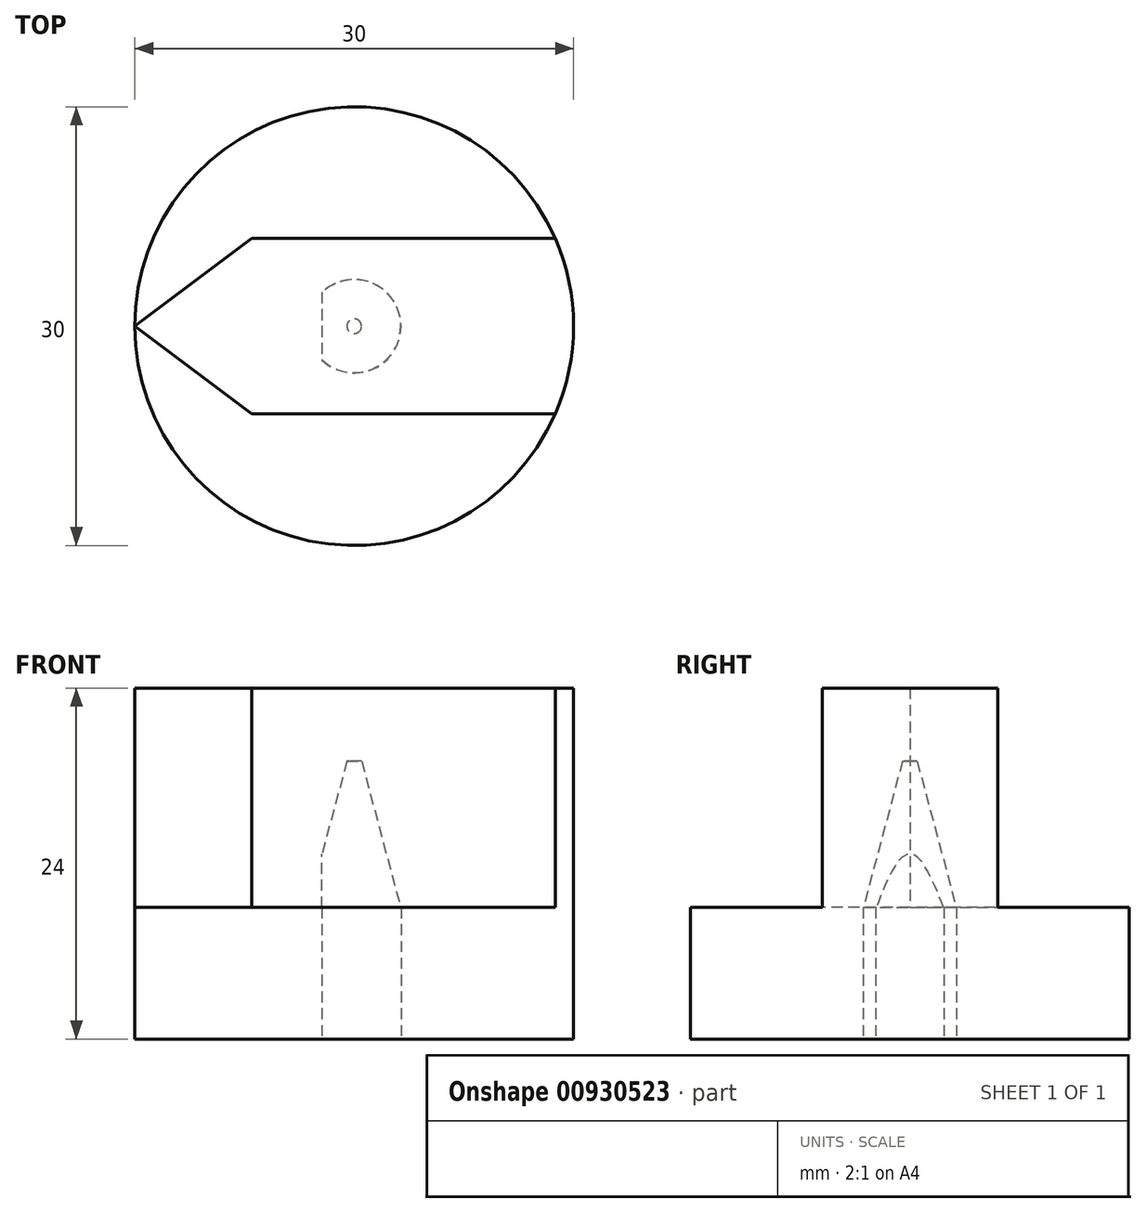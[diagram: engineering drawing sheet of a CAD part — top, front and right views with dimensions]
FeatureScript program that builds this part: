
annotation { "Feature Type Name" : "Feature", "Feature Type Description" : "" }
export const myFeature = defineFeature(function(context is Context, id is Id, definition is map)
    precondition{}
    {
        {
            var Q0;
            Q0=qCreatedBy(makeId("Top.planeOp"),FACE);
            var sketch = newSketch(context, id + "F0", { "sketchPlane" : qUnion([Q0])});
            skCircle(sketch, "E0", {"center": v(0, 0) * mm, "radius": 3.2 * mm, "construction": true});
            skLineSegment(sketch, "E1", {"start": v(-2.2, 2.32) * mm, "end": v(-2.2, -2.32) * mm});
            skLineSegment(sketch, "E2", {"start": v(3.2, 0) * mm, "end": v(-2.2, 0) * mm, "construction": true});
            skArc(sketch, "E3", {"start": v(-2.2, -2.32) * mm, "mid": v(3.2, 0) * mm, "end": v(-2.2, 2.32) * mm});
            skCircle(sketch, "E4", {"center": v(0, 0) * mm, "radius": 15 * mm});
            skSolve(sketch);
        }
        {
            var Q0;
            Q0 = qSketchRegion(id + "F0", true);
            extrude(context, id + "F1", {"entities" : qUnion([Q0]), "depth" : 9 * mm, "offsetDistance" : 25 * mm});
        }
        {
            var Q0;
            Q0=makeQuery(id+"F1.opExtrude","CAP_FACE",FACE,{"disambiguationData":[OSD([sQuery(id+"F0.wireOp",EDGE,"E1"),sQuery(id+"F0.wireOp",EDGE,"E3"),sQuery(id+"F0.wireOp",EDGE,"E4")])],"isStart":false});
            var sketch = newSketch(context, id + "F2", { "sketchPlane" : qUnion([Q0])});
            skLineSegment(sketch, "E5", {"start": v(-15, 0) * mm, "end": v(-7, 6) * mm});
            skLineSegment(sketch, "E6", {"start": v(-7, 6) * mm, "end": v(13.75, 6) * mm});
            skArc(sketch, "E7", {"start": v(15, 0) * mm, "mid": v(14.68, 3.06) * mm, "end": v(13.75, 6) * mm});
            skLineSegment(sketch, "E8", {"start": v(-15, 0) * mm, "end": v(15, 0) * mm, "construction": true});
            skLineSegment(sketch, "E9.MirrorCS", {"start": v(-15, 0) * mm, "end": v(-7, -6) * mm});
            skLineSegment(sketch, "E10.MirrorCS", {"start": v(-7, -6) * mm, "end": v(13.75, -6) * mm});
            skArc(sketch, "E11.MirrorCS", {"start": v(15, 0) * mm, "mid": v(14.68, -3.06) * mm, "end": v(13.75, -6) * mm});
            skCircle(sketch, "E12", {"center": v(0, 0) * mm, "radius": 0.5 * mm});
            skSolve(sketch);
        }
        {
            var Q0;
            Q0 = qSketchRegion(id + "F2", true);
            extrude(context, id + "F3", {"entities" : qUnion([Q0]), "operationType" : NewBodyOperationType.ADD, "depth" : 10 * mm, "offsetDistance" : 25 * mm});
        }
        {
            var Q0;
            Q0=makeQuery(id+"F3.opExtrude","CAP_EDGE",EDGE,{"disambiguationData":[OSD([sQuery(id+"F2.wireOp",EDGE,"E12")])],"isStart":true});
            chamfer(context, id + "F4", {"entities" : qUnion([Q0]), "chamferType" : ChamferType.OFFSET_ANGLE, "width" : 10 * mm, "oppositeDirection" : true, "angle" : 15 * degree, "tangentPropagation" : true});
        }
        {
            var Q0;
            Q0=makeQuery(id+"F3.opExtrude","CAP_FACE",FACE,{"disambiguationData":[OSD([sQuery(id+"F2.wireOp",EDGE,"E5"),sQuery(id+"F2.wireOp",EDGE,"E6"),sQuery(id+"F2.wireOp",EDGE,"E7"),sQuery(id+"F2.wireOp",EDGE,"E9.MirrorCS"),sQuery(id+"F2.wireOp",EDGE,"E10.MirrorCS"),sQuery(id+"F2.wireOp",EDGE,"E11.MirrorCS"),sQuery(id+"F2.wireOp",EDGE,"E12")])],"isStart":false});
            var sketch = newSketch(context, id + "F5", { "sketchPlane" : qUnion([Q0])});
            skLineSegment(sketch, "E13", {"start": v(-15, 0) * mm, "end": v(-7, 6) * mm});
            skLineSegment(sketch, "E14", {"start": v(-7, 6) * mm, "end": v(13.75, 6) * mm});
            skLineSegment(sketch, "E15", {"start": v(-15, 0) * mm, "end": v(-7, -6) * mm});
            skLineSegment(sketch, "E16", {"start": v(-7, -6) * mm, "end": v(13.75, -6) * mm});
            skArc(sketch, "E17", {"start": v(13.75, -6) * mm, "mid": v(15, 0) * mm, "end": v(13.75, 6) * mm});
            skSolve(sketch);
        }
        {
            var Q0;
            Q0 = qSketchRegion(id + "F5", true);
            extrude(context, id + "F6", {"entities" : qUnion([Q0]), "operationType" : NewBodyOperationType.ADD, "depth" : 5 * mm, "offsetDistance" : 25 * mm});
        }
    });
